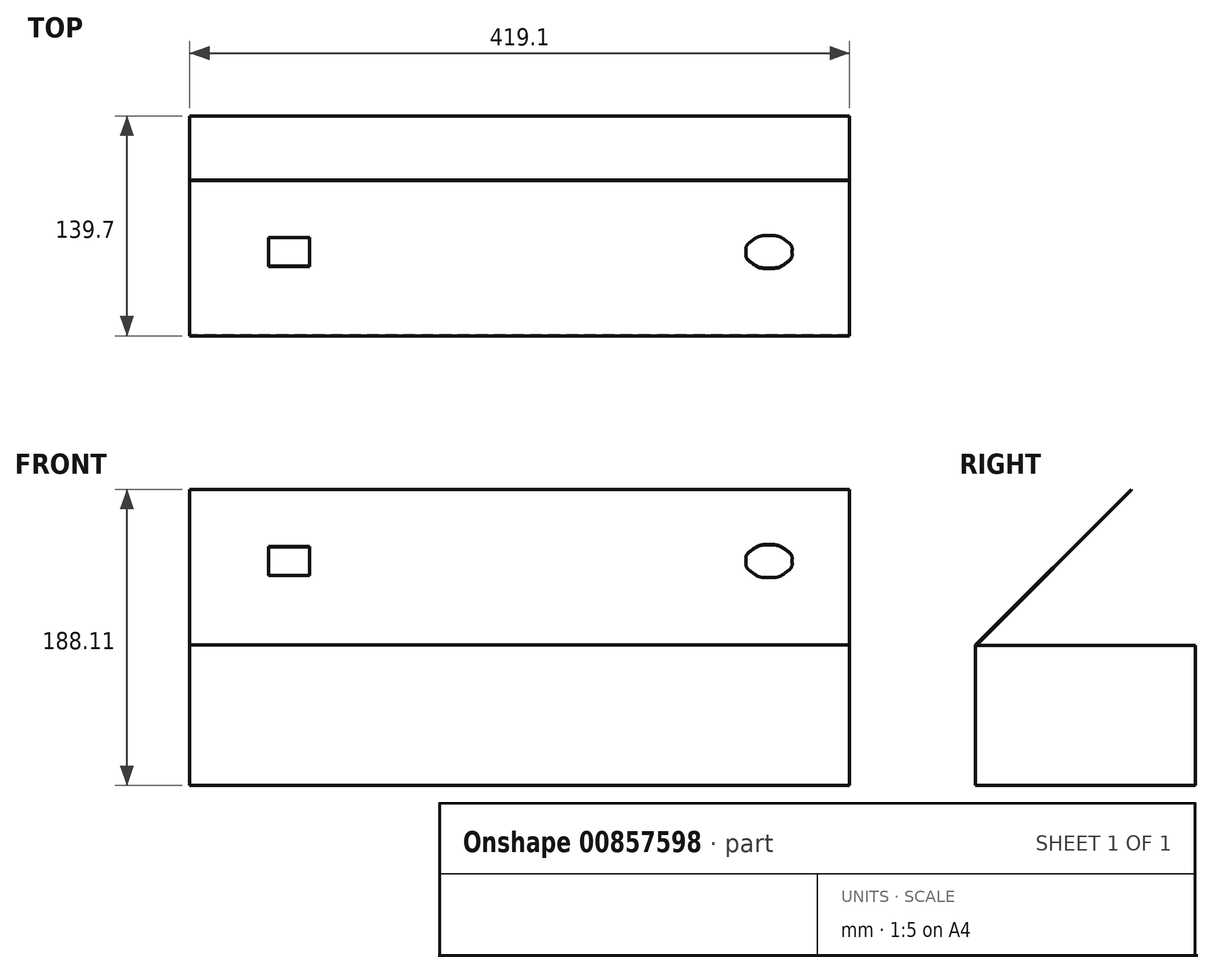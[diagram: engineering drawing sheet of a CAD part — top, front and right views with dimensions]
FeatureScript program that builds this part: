
annotation { "Feature Type Name" : "Feature", "Feature Type Description" : "" }
export const myFeature = defineFeature(function(context is Context, id is Id, definition is map)
    precondition{}
    {
        {
            var Q0;
            Q0=qCreatedBy(makeId("Right.planeOp"),FACE);
            var sketch = newSketch(context, id + "F0", { "sketchPlane" : qUnion([Q0])});
            skLineSegment(sketch, "E0.bottom", {"start": v(0, 0) * mm, "end": v(-139.7, 0) * mm});
            skLineSegment(sketch, "E0.top", {"start": v(0, 88.9) * mm, "end": v(-139.3, 88.9) * mm});
            skLineSegment(sketch, "E0.left", {"start": v(0, 0) * mm, "end": v(0, 88.9) * mm});
            skLineSegment(sketch, "E0.right", {"start": v(-139.7, 0) * mm, "end": v(-139.7, 89.32) * mm});
            skLineSegment(sketch, "E1", {"start": v(-139.7, 89.32) * mm, "end": v(-40.92, 188.1) * mm});
            skLineSegment(sketch, "E2", {"start": v(-40.92, 188.1) * mm, "end": v(-40.63, 187.82) * mm});
            skLineSegment(sketch, "E3", {"start": v(-40.63, 187.82) * mm, "end": v(-139.3, 89.15) * mm});
            skLineSegment(sketch, "E4", {"start": v(-139.3, 88.9) * mm, "end": v(-139.3, 89.15) * mm});
            skLineSegment(sketch, "E5", {"start": v(-139.3, 88.9) * mm, "end": v(-139.7, 88.9) * mm, "construction": true});
            skSolve(sketch);
        }
        {
            var Q0;
            Q0=qSketchRegion(id+"F0",true);
            extrude(context, id + "F1", {"entities" : qUnion([Q0]), "endBound" : BoundingType.SYMMETRIC, "depth" : 419.1 * mm, "offsetDistance" : 25.4 * mm});
        }
        {
            var Q0;
            Q0=makeQuery(id+"F1.opExtrude","SWEPT_FACE",FACE,{"disambiguationData":[OSD([sQuery(id+"F0.wireOp",EDGE,"E1")])]});
            var sketch = newSketch(context, id + "F2", { "sketchPlane" : qUnion([Q0])});
            skLineSegment(sketch, "E6", {"start": v(-159.6, 26.64) * mm, "end": v(-133.41, 26.64) * mm});
            skLineSegment(sketch, "E7", {"start": v(-159.6, 52.83) * mm, "end": v(-159.6, 26.64) * mm});
            skLineSegment(sketch, "E8", {"start": v(-133.41, 52.83) * mm, "end": v(-159.6, 52.83) * mm});
            skLineSegment(sketch, "E9", {"start": v(-133.41, 26.64) * mm, "end": v(-133.41, 52.83) * mm});
            skLineSegment(sketch, "E10", {"start": v(-210, -36.46) * mm, "end": v(-210, 102.44) * mm, "construction": true});
            skLineSegment(sketch, "E11", {"start": v(209.1, -36.46) * mm, "end": v(209.1, 102.44) * mm, "construction": true});
            skLineSegment(sketch, "E12", {"start": v(-210, 102.44) * mm, "end": v(209.1, 102.44) * mm, "construction": true});
            skLineSegment(sketch, "E13", {"start": v(209.1, -36.46) * mm, "end": v(-210, -36.46) * mm, "construction": true});
            skFitSpline(sketch, "E14", {"points": [v(158.3, 54.42) * mm, v(154.45, 54.42) * mm, v(150.63, 52.84) * mm, v(147.9, 50.12) * mm]});
            skFitSpline(sketch, "E15", {"points": [v(147.9, 50.12) * mm, v(145.19, 47.4) * mm, v(143.6, 43.58) * mm, v(143.6, 39.74) * mm, v(143.6, 35.9) * mm, v(145.19, 32.07) * mm, v(147.9, 29.35) * mm]});
            skFitSpline(sketch, "E16", {"points": [v(147.9, 29.35) * mm, v(150.63, 26.64) * mm, v(154.45, 25.05) * mm, v(158.3, 25.05) * mm, v(162.14, 25.05) * mm, v(165.96, 26.64) * mm, v(168.67, 29.35) * mm]});
            skFitSpline(sketch, "E17", {"points": [v(168.67, 29.35) * mm, v(171.4, 32.07) * mm, v(172.98, 35.9) * mm, v(172.98, 39.74) * mm, v(172.98, 43.58) * mm, v(171.4, 47.4) * mm, v(168.67, 50.12) * mm]});
            skFitSpline(sketch, "E18", {"points": [v(168.67, 50.12) * mm, v(165.96, 52.84) * mm, v(162.14, 54.42) * mm, v(158.3, 54.42) * mm]});
            skSolve(sketch);
        }
        {
            var Q0;
            Q0=qSketchRegion(id+"F2",true);
            var Q1;
            Q1=makeQuery(id+"F1.opExtrude","SWEPT_FACE",FACE,{"disambiguationData":[OSD([sQuery(id+"F0.wireOp",EDGE,"E3")])]});
            extrude(context, id + "F3", {"entities" : qUnion([Q0]), "operationType" : NewBodyOperationType.REMOVE, "endBound" : BoundingType.UP_TO_SURFACE, "oppositeDirection" : true, "depth" : 25.4 * mm, "endBoundEntityFace" : qUnion([Q1]), "offsetDistance" : 25.4 * mm});
        }
    });
